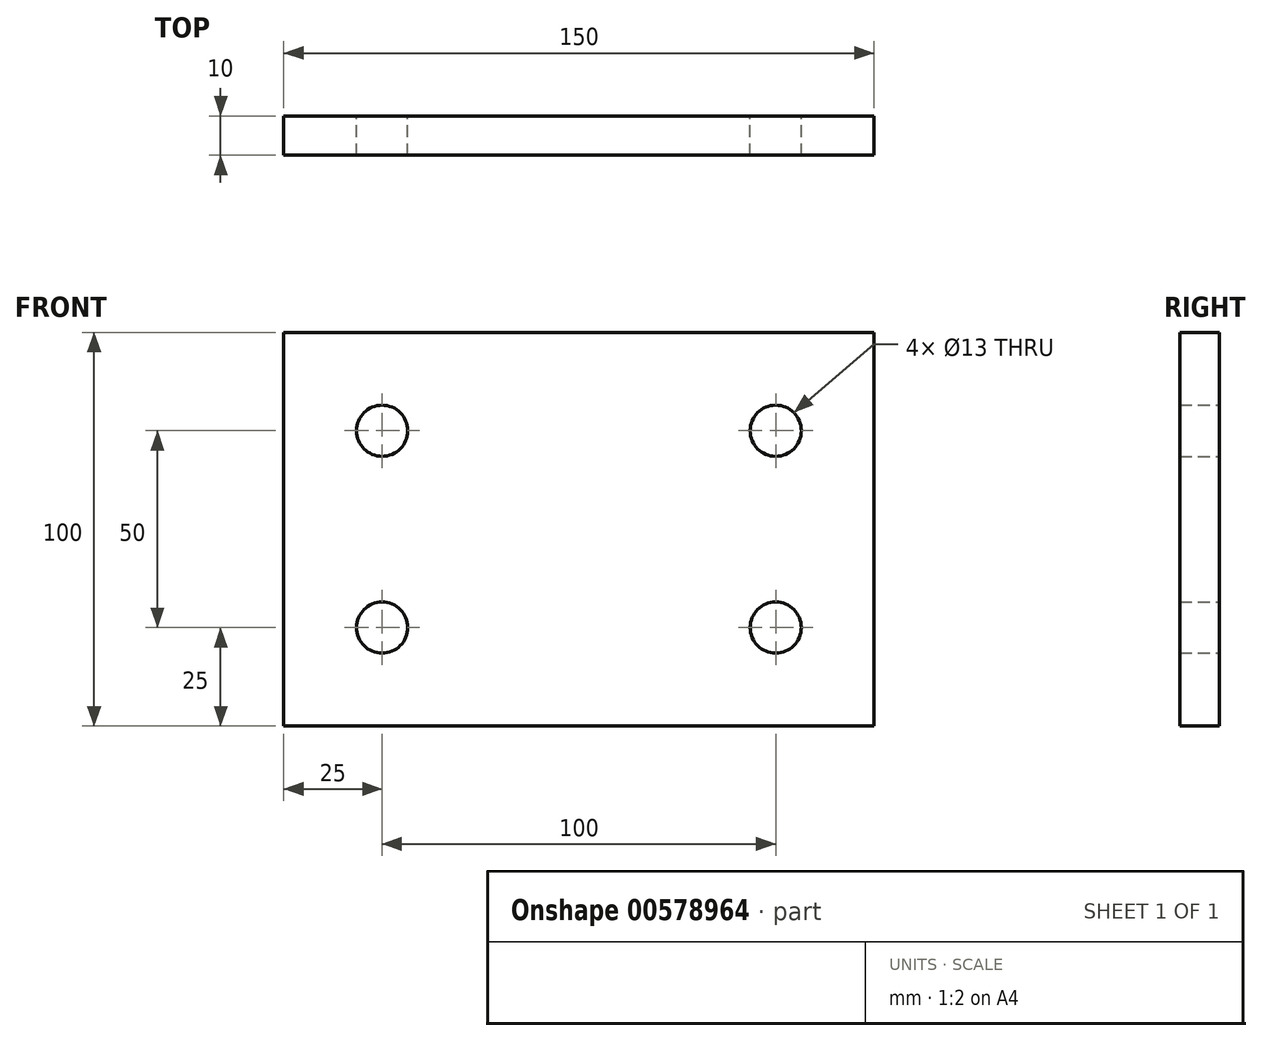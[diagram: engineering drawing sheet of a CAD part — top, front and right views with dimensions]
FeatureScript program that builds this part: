
annotation { "Feature Type Name" : "Feature", "Feature Type Description" : "" }
export const myFeature = defineFeature(function(context is Context, id is Id, definition is map)
    precondition{}
    {
        {
            var Q0;
            Q0=qCreatedBy(makeId("Front.planeOp"),FACE);
            var sketch = newSketch(context, id + "F0", { "sketchPlane" : qUnion([Q0])});
            skLineSegment(sketch, "E0.bottom", {"start": v(75, 50) * mm, "end": v(-75, 50) * mm});
            skLineSegment(sketch, "E0.top", {"start": v(75, -50) * mm, "end": v(-75, -50) * mm});
            skLineSegment(sketch, "E0.left", {"start": v(75, 50) * mm, "end": v(75, -50) * mm});
            skLineSegment(sketch, "E0.right", {"start": v(-75, 50) * mm, "end": v(-75, -50) * mm});
            skPoint(sketch, "E0.middle", {"position": v(0, 0) * mm});
            skCircle(sketch, "E1", {"center": v(50, -25) * mm, "radius": 6.5 * mm});
            skCircle(sketch, "E2", {"center": v(50, 25) * mm, "radius": 6.5 * mm});
            skCircle(sketch, "E3", {"center": v(-50, 25) * mm, "radius": 6.5 * mm});
            skCircle(sketch, "E4", {"center": v(-50, -25) * mm, "radius": 6.5 * mm});
            skSolve(sketch);
        }
        {
            var Q0;
            Q0=makeQuery(id+"F0.imprint","IMPRINT",FACE,{"disambiguationData":[TD([[makeQuery(id+"F0.imprint","IMPRINT",EDGE,{"derivedFrom":sQuery(id+"F0.wireOp",EDGE,"E0.bottom")}),1.0]])]});
            extrude(context, id + "F1", {"entities" : qUnion([Q0]), "endBound" : BoundingType.SYMMETRIC, "depth" : 10 * mm, "offsetDistance" : 25 * mm});
        }
    });
